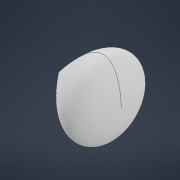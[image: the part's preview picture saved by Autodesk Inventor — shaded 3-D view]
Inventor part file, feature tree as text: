
AUTODESK INVENTOR PART (.ipt)
format: ipt  version: 2022 (Build 260153000, 153)  size: 443,392 bytes
history: native  units: in
note: dims shown in document units (in); Inventor stores cm internally (conversion verified against a paired STEP export)
features: revolve x1, sketch x1, other x1
ambient origin geometry x8: Origin, YZ Plane, XZ Plane, XY Plane, X Axis, Y Axis, Z Axis, Center Point
bodies: Solid1 (feature_tree)
feature tree (3):
  revolve  "Revolution1"  Angle=90.0deg
  sketch  "Sketch1"  dims[d0=0.0in d1=0.7874in d2=90.0deg]
  other  "2D Equation Curve1"
